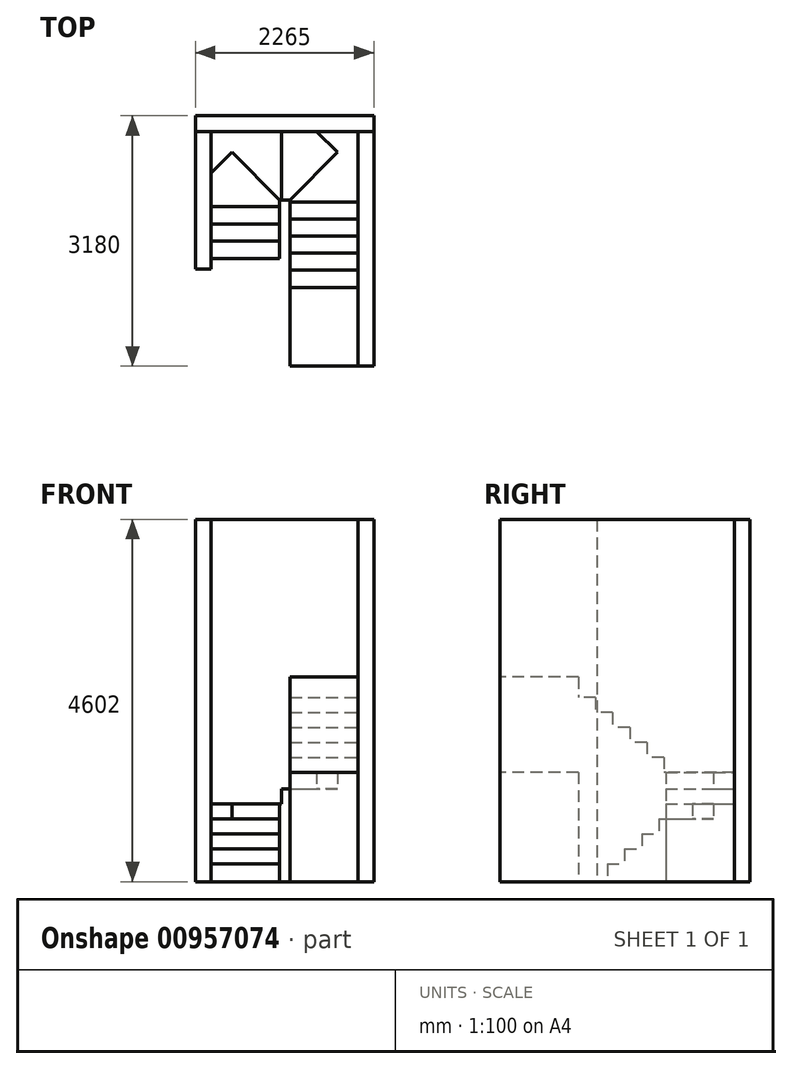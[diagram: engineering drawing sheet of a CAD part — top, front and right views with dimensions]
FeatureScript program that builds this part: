
annotation { "Feature Type Name" : "Feature", "Feature Type Description" : "" }
export const myFeature = defineFeature(function(context is Context, id is Id, definition is map)
    precondition{}
    {
        {
            var Q0;
            Q0=qCreatedBy(makeId("Top.planeOp"),FACE);
            var sketch = newSketch(context, id + "F0", { "sketchPlane" : qUnion([Q0])});
            skLineSegment(sketch, "E0", {"start": v(0, 0) * mm, "end": v(0, 1745) * mm});
            skLineSegment(sketch, "E1", {"start": v(0, 1745) * mm, "end": v(1865, 1745) * mm});
            skLineSegment(sketch, "E2", {"start": v(1865, 1745) * mm, "end": v(1865, -235) * mm});
            skLineSegment(sketch, "E3", {"start": v(870, 0) * mm, "end": v(870, 875) * mm});
            skLineSegment(sketch, "E4", {"start": v(870, 875) * mm, "end": v(1000, 875) * mm});
            skLineSegment(sketch, "E5", {"start": v(1000, 875) * mm, "end": v(1000, -235) * mm});
            skLineSegment(sketch, "E6", {"start": v(0, 130) * mm, "end": v(870, 130) * mm});
            skLineSegment(sketch, "E7", {"start": v(0, 350) * mm, "end": v(870, 350) * mm});
            skLineSegment(sketch, "E8", {"start": v(0, 570) * mm, "end": v(870, 570) * mm});
            skLineSegment(sketch, "E9", {"start": v(435, 130) * mm, "end": v(435, 350) * mm, "construction": true});
            skLineSegment(sketch, "E10", {"start": v(435, 350) * mm, "end": v(435, 570) * mm, "construction": true});
            skLineSegment(sketch, "E11", {"start": v(870, 790) * mm, "end": v(0, 790) * mm});
            skLineSegment(sketch, "E12", {"start": v(435, 570) * mm, "end": v(435, 790) * mm, "construction": true});
            skLineSegment(sketch, "E13", {"start": v(870, 875) * mm, "end": v(265, 1480) * mm});
            skLineSegment(sketch, "E14", {"start": v(265, 1480) * mm, "end": v(0, 1215) * mm});
            skLineSegment(sketch, "E15", {"start": v(895, 875) * mm, "end": v(895, 1745) * mm});
            skLineSegment(sketch, "E16", {"start": v(1000, 875) * mm, "end": v(1605, 1480) * mm});
            skLineSegment(sketch, "E17", {"start": v(1605, 1480) * mm, "end": v(1340, 1745) * mm});
            skLineSegment(sketch, "E18", {"start": v(1000, 850) * mm, "end": v(1865, 850) * mm});
            skLineSegment(sketch, "E19", {"start": v(1000, 633) * mm, "end": v(1865, 633) * mm});
            skLineSegment(sketch, "E20", {"start": v(1000, 416) * mm, "end": v(1865, 416) * mm});
            skLineSegment(sketch, "E21", {"start": v(1000, 199) * mm, "end": v(1865, 199) * mm});
            skLineSegment(sketch, "E22", {"start": v(1000, -18) * mm, "end": v(1865, -18) * mm});
            skLineSegment(sketch, "E23", {"start": v(1432.5, 850) * mm, "end": v(1432.5, 633) * mm, "construction": true});
            skLineSegment(sketch, "E24", {"start": v(1432.5, 633) * mm, "end": v(1432.5, 416) * mm, "construction": true});
            skLineSegment(sketch, "E25", {"start": v(1432.5, 416) * mm, "end": v(1432.5, 199) * mm, "construction": true});
            skLineSegment(sketch, "E26", {"start": v(1432.5, 199) * mm, "end": v(1432.5, -18) * mm, "construction": true});
            skLineSegment(sketch, "E27", {"start": v(1432.5, -18) * mm, "end": v(1432.5, -235) * mm, "construction": true});
            skLineSegment(sketch, "E28.trimOffspring", {"start": v(870, 0) * mm, "end": v(0, 0) * mm});
            skLineSegment(sketch, "E29", {"start": v(1000, -235) * mm, "end": v(1865, -235) * mm});
            skSolve(sketch);
        }
        {
            var Q0;
            {var subQ0=sQuery(id+"F0.wireOp",EDGE,"E13");Q0=makeQuery(id+"F0.imprint","IMPRINT",FACE,{"disambiguationData":[TD([[makeQuery(id+"F0.imprint","IMPRINT",EDGE,{"derivedFrom":subQ0}),-1.0]])]});}
            extrude(context, id + "F1", {"entities" : qUnion([Q0]), "depth" : 987 * mm, "offsetDistance" : 25 * mm});
        }
        {
            var Q0;
            {var subQ1=sQuery(id+"F0.wireOp",EDGE,"E11");Q0=makeQuery(id+"F0.imprint","IMPRINT",FACE,{"disambiguationData":[TD([[makeQuery(id+"F0.imprint","IMPRINT",EDGE,{"derivedFrom":subQ1}),-1.0]])]});}
            var Q1;
            Q1=makeQuery(id+"F1.opExtrude","CAP_FACE",FACE,{"disambiguationData":[OSD([sQuery(id+"F0.wireOp",EDGE,"E0"),sQuery(id+"F0.wireOp",EDGE,"E1"),sQuery(id+"F0.wireOp",EDGE,"E4"),sQuery(id+"F0.wireOp",EDGE,"E13"),sQuery(id+"F0.wireOp",EDGE,"E14"),sQuery(id+"F0.wireOp",EDGE,"E15")])],"isStart":false});
            extrude(context, id + "F2", {"entities" : qUnion([Q0]), "operationType" : NewBodyOperationType.ADD, "endBound" : BoundingType.UP_TO_SURFACE, "depth" : 25 * mm, "endBoundEntityFace" : qUnion([Q1]), "hasOffset" : true, "offsetDistance" : 190 * mm});
        }
        {
            var Q0;
            {var subQ0=sQuery(id+"F0.wireOp",EDGE,"E8");Q0=makeQuery(id+"F0.imprint","IMPRINT",FACE,{"disambiguationData":[TD([[makeQuery(id+"F0.imprint","IMPRINT",EDGE,{"derivedFrom":subQ0}),1.0]])]});}
            var Q1;
            Q1=makeQuery(id+"F2.opExtrude","CAP_FACE",FACE,{"disambiguationData":[OSD([sQuery(id+"F0.wireOp",EDGE,"E0"),sQuery(id+"F0.wireOp",EDGE,"E3"),sQuery(id+"F0.wireOp",EDGE,"E11"),sQuery(id+"F0.wireOp",EDGE,"E13"),sQuery(id+"F0.wireOp",EDGE,"E14")])],"isStart":false});
            extrude(context, id + "F3", {"entities" : qUnion([Q0]), "operationType" : NewBodyOperationType.ADD, "endBound" : BoundingType.UP_TO_SURFACE, "depth" : 25 * mm, "endBoundEntityFace" : qUnion([Q1]), "hasOffset" : true, "offsetDistance" : 190 * mm});
        }
        {
            var Q0;
            {var subQ0=sQuery(id+"F0.wireOp",EDGE,"E7");Q0=makeQuery(id+"F0.imprint","IMPRINT",FACE,{"disambiguationData":[TD([[makeQuery(id+"F0.imprint","IMPRINT",EDGE,{"derivedFrom":subQ0}),1.0]])]});}
            var Q1;
            Q1=makeQuery(id+"F3.opExtrude","CAP_FACE",FACE,{"disambiguationData":[OSD([sQuery(id+"F0.wireOp",EDGE,"E0"),sQuery(id+"F0.wireOp",EDGE,"E3"),sQuery(id+"F0.wireOp",EDGE,"E8"),sQuery(id+"F0.wireOp",EDGE,"E11")])],"isStart":false});
            extrude(context, id + "F4", {"entities" : qUnion([Q0]), "operationType" : NewBodyOperationType.ADD, "endBound" : BoundingType.UP_TO_SURFACE, "depth" : 25 * mm, "endBoundEntityFace" : qUnion([Q1]), "hasOffset" : true, "offsetDistance" : 190 * mm});
        }
        {
            var Q0;
            {var subQ0=sQuery(id+"F0.wireOp",EDGE,"E6");Q0=makeQuery(id+"F0.imprint","IMPRINT",FACE,{"disambiguationData":[TD([[makeQuery(id+"F0.imprint","IMPRINT",EDGE,{"derivedFrom":subQ0}),1.0]])]});}
            var Q1;
            Q1=makeQuery(id+"F4.opExtrude","CAP_FACE",FACE,{"disambiguationData":[OSD([sQuery(id+"F0.wireOp",EDGE,"E0"),sQuery(id+"F0.wireOp",EDGE,"E3"),sQuery(id+"F0.wireOp",EDGE,"E7"),sQuery(id+"F0.wireOp",EDGE,"E8")])],"isStart":false});
            extrude(context, id + "F5", {"entities" : qUnion([Q0]), "operationType" : NewBodyOperationType.ADD, "endBound" : BoundingType.UP_TO_SURFACE, "depth" : 25 * mm, "endBoundEntityFace" : qUnion([Q1]), "hasOffset" : true, "offsetDistance" : 190 * mm});
        }
        {
            var Q0;
            {var subQ1=sQuery(id+"F0.wireOp",EDGE,"E15");Q0=makeQuery(id+"F0.imprint","IMPRINT",FACE,{"disambiguationData":[TD([[makeQuery(id+"F0.imprint","IMPRINT",EDGE,{"derivedFrom":subQ1}),-1.0]])]});}
            var Q1;
            Q1=makeQuery(id+"F1.opExtrude","CAP_FACE",FACE,{"disambiguationData":[OSD([sQuery(id+"F0.wireOp",EDGE,"E0"),sQuery(id+"F0.wireOp",EDGE,"E1"),sQuery(id+"F0.wireOp",EDGE,"E4"),sQuery(id+"F0.wireOp",EDGE,"E13"),sQuery(id+"F0.wireOp",EDGE,"E14"),sQuery(id+"F0.wireOp",EDGE,"E15")])],"isStart":false});
            extrude(context, id + "F6", {"entities" : qUnion([Q0]), "operationType" : NewBodyOperationType.ADD, "endBound" : BoundingType.UP_TO_SURFACE, "depth" : 25 * mm, "endBoundEntityFace" : qUnion([Q1]), "hasOffset" : true, "offsetDistance" : 190 * mm, "offsetOppositeDirection" : true});
        }
        {
            var Q0;
            {var subQ0=sQuery(id+"F0.wireOp",EDGE,"E16");Q0=makeQuery(id+"F0.imprint","IMPRINT",FACE,{"disambiguationData":[TD([[makeQuery(id+"F0.imprint","IMPRINT",EDGE,{"derivedFrom":subQ0}),-1.0]])]});}
            var Q1;
            Q1=makeQuery(id+"F1.opExtrude","CAP_FACE",FACE,{"disambiguationData":[OSD([sQuery(id+"F0.wireOp",EDGE,"E0"),sQuery(id+"F0.wireOp",EDGE,"E1"),sQuery(id+"F0.wireOp",EDGE,"E4"),sQuery(id+"F0.wireOp",EDGE,"E13"),sQuery(id+"F0.wireOp",EDGE,"E14"),sQuery(id+"F0.wireOp",EDGE,"E15")])],"isStart":false});
            extrude(context, id + "F7", {"entities" : qUnion([Q0]), "operationType" : NewBodyOperationType.ADD, "endBound" : BoundingType.UP_TO_SURFACE, "depth" : 25 * mm, "endBoundEntityFace" : qUnion([Q1]), "hasOffset" : true, "offsetDistance" : 405 * mm, "offsetOppositeDirection" : true});
        }
        {
            var Q0;
            {var subQ0=sQuery(id+"F0.wireOp",EDGE,"E18");Q0=makeQuery(id+"F0.imprint","IMPRINT",FACE,{"disambiguationData":[TD([[makeQuery(id+"F0.imprint","IMPRINT",EDGE,{"derivedFrom":subQ0}),-1.0]])]});}
            var Q1;
            Q1=makeQuery(id+"F7.opExtrude","CAP_FACE",FACE,{"disambiguationData":[OSD([sQuery(id+"F0.wireOp",EDGE,"E1"),sQuery(id+"F0.wireOp",EDGE,"E2"),sQuery(id+"F0.wireOp",EDGE,"E5"),sQuery(id+"F0.wireOp",EDGE,"E16"),sQuery(id+"F0.wireOp",EDGE,"E17"),sQuery(id+"F0.wireOp",EDGE,"E18")])],"isStart":false});
            extrude(context, id + "F8", {"entities" : qUnion([Q0]), "operationType" : NewBodyOperationType.ADD, "endBound" : BoundingType.UP_TO_SURFACE, "depth" : 25 * mm, "endBoundEntityFace" : qUnion([Q1]), "hasOffset" : true, "offsetDistance" : 190 * mm, "offsetOppositeDirection" : true});
        }
        {
            var Q0;
            {var subQ0=sQuery(id+"F0.wireOp",EDGE,"E19");Q0=makeQuery(id+"F0.imprint","IMPRINT",FACE,{"disambiguationData":[TD([[makeQuery(id+"F0.imprint","IMPRINT",EDGE,{"derivedFrom":subQ0}),-1.0]])]});}
            var Q1;
            Q1=makeQuery(id+"F8.opExtrude","CAP_FACE",FACE,{"disambiguationData":[OSD([sQuery(id+"F0.wireOp",EDGE,"E2"),sQuery(id+"F0.wireOp",EDGE,"E5"),sQuery(id+"F0.wireOp",EDGE,"E18"),sQuery(id+"F0.wireOp",EDGE,"E19")])],"isStart":false});
            extrude(context, id + "F9", {"entities" : qUnion([Q0]), "operationType" : NewBodyOperationType.ADD, "endBound" : BoundingType.UP_TO_SURFACE, "depth" : 25 * mm, "endBoundEntityFace" : qUnion([Q1]), "hasOffset" : true, "offsetDistance" : 190 * mm, "offsetOppositeDirection" : true});
        }
        {
            var Q0;
            {var subQ0=sQuery(id+"F0.wireOp",EDGE,"E20");Q0=makeQuery(id+"F0.imprint","IMPRINT",FACE,{"disambiguationData":[TD([[makeQuery(id+"F0.imprint","IMPRINT",EDGE,{"derivedFrom":subQ0}),-1.0]])]});}
            var Q1;
            Q1=makeQuery(id+"F9.opExtrude","CAP_FACE",FACE,{"disambiguationData":[OSD([sQuery(id+"F0.wireOp",EDGE,"E2"),sQuery(id+"F0.wireOp",EDGE,"E5"),sQuery(id+"F0.wireOp",EDGE,"E19"),sQuery(id+"F0.wireOp",EDGE,"E20")])],"isStart":false});
            extrude(context, id + "F10", {"entities" : qUnion([Q0]), "operationType" : NewBodyOperationType.ADD, "endBound" : BoundingType.UP_TO_SURFACE, "depth" : 25 * mm, "endBoundEntityFace" : qUnion([Q1]), "hasOffset" : true, "offsetDistance" : 190 * mm, "offsetOppositeDirection" : true});
        }
        {
            var Q0;
            {var subQ0=sQuery(id+"F0.wireOp",EDGE,"E21");Q0=makeQuery(id+"F0.imprint","IMPRINT",FACE,{"disambiguationData":[TD([[makeQuery(id+"F0.imprint","IMPRINT",EDGE,{"derivedFrom":subQ0}),-1.0]])]});}
            var Q1;
            Q1=makeQuery(id+"F10.opExtrude","CAP_FACE",FACE,{"disambiguationData":[OSD([sQuery(id+"F0.wireOp",EDGE,"E2"),sQuery(id+"F0.wireOp",EDGE,"E5"),sQuery(id+"F0.wireOp",EDGE,"E20"),sQuery(id+"F0.wireOp",EDGE,"E21")])],"isStart":false});
            extrude(context, id + "F11", {"entities" : qUnion([Q0]), "operationType" : NewBodyOperationType.ADD, "endBound" : BoundingType.UP_TO_SURFACE, "depth" : 25 * mm, "endBoundEntityFace" : qUnion([Q1]), "hasOffset" : true, "offsetDistance" : 190 * mm, "offsetOppositeDirection" : true});
        }
        {
            var Q0;
            {var subQ2=sQuery(id+"F0.wireOp",EDGE,"E22");Q0=makeQuery(id+"F0.imprint","IMPRINT",FACE,{"disambiguationData":[TD([[makeQuery(id+"F0.imprint","IMPRINT",EDGE,{"derivedFrom":subQ2}),-1.0]])]});}
            var Q1;
            Q1=makeQuery(id+"F11.opExtrude","CAP_FACE",FACE,{"disambiguationData":[OSD([sQuery(id+"F0.wireOp",EDGE,"E2"),sQuery(id+"F0.wireOp",EDGE,"E5"),sQuery(id+"F0.wireOp",EDGE,"E21"),sQuery(id+"F0.wireOp",EDGE,"E22")])],"isStart":false});
            extrude(context, id + "F12", {"entities" : qUnion([Q0]), "operationType" : NewBodyOperationType.ADD, "endBound" : BoundingType.UP_TO_SURFACE, "depth" : 25 * mm, "endBoundEntityFace" : qUnion([Q1]), "hasOffset" : true, "offsetDistance" : 190 * mm, "offsetOppositeDirection" : true});
        }
        {
            var Q0;
            Q0=makeQuery(id+"F7.opExtrude","CAP_FACE",FACE,{"disambiguationData":[OSD([sQuery(id+"F0.wireOp",EDGE,"E1"),sQuery(id+"F0.wireOp",EDGE,"E2"),sQuery(id+"F0.wireOp",EDGE,"E5"),sQuery(id+"F0.wireOp",EDGE,"E16"),sQuery(id+"F0.wireOp",EDGE,"E17"),sQuery(id+"F0.wireOp",EDGE,"E18")])],"isStart":false});
            var sketch = newSketch(context, id + "F13", { "sketchPlane" : qUnion([Q0])});
            skLineSegment(sketch, "E30.bottom", {"start": v(1865, -235) * mm, "end": v(1000, -235) * mm});
            skLineSegment(sketch, "E30.top", {"start": v(1865, -1235) * mm, "end": v(1000, -1235) * mm});
            skLineSegment(sketch, "E30.left", {"start": v(1865, -235) * mm, "end": v(1865, -1235) * mm});
            skLineSegment(sketch, "E30.right", {"start": v(1000, -235) * mm, "end": v(1000, -1235) * mm});
            skSolve(sketch);
        }
        {
            var Q0;
            Q0 = qSketchRegion(id + "F13", true);
            extrude(context, id + "F14", {"entities" : qUnion([Q0]), "operationType" : NewBodyOperationType.ADD, "depth" : 1210 * mm, "offsetDistance" : 25 * mm});
        }
        {
            var Q0;
            Q0=qCreatedBy(makeId("Top.planeOp"),FACE);
            var sketch = newSketch(context, id + "F15", { "sketchPlane" : qUnion([Q0])});
            skLineSegment(sketch, "E31.bottom", {"start": v(0, 1745) * mm, "end": v(-200, 1745) * mm});
            skLineSegment(sketch, "E31.top", {"start": v(0, 0) * mm, "end": v(-200, 0) * mm});
            skLineSegment(sketch, "E31.left", {"start": v(0, 1745) * mm, "end": v(0, 0) * mm});
            skLineSegment(sketch, "E31.right", {"start": v(-200, 1745) * mm, "end": v(-200, 0) * mm});
            skSolve(sketch);
        }
        {
            var Q0;
            Q0 = qSketchRegion(id + "F15", true);
            var Q1;
            Q1=makeQuery(id+"F14.opExtrude","CAP_FACE",FACE,{"disambiguationData":[OSD([sQuery(id+"F13.wireOp",EDGE,"E30.bottom"),sQuery(id+"F13.wireOp",EDGE,"E30.top"),sQuery(id+"F13.wireOp",EDGE,"E30.left"),sQuery(id+"F13.wireOp",EDGE,"E30.right")])],"isStart":false});
            extrude(context, id + "F16", {"entities" : qUnion([Q0]), "endBound" : BoundingType.UP_TO_SURFACE, "depth" : 25 * mm, "endBoundEntityFace" : qUnion([Q1]), "hasOffset" : true, "offsetDistance" : 2000 * mm, "offsetOppositeDirection" : true});
        }
        {
            var Q0;
            Q0=qCreatedBy(makeId("Top.planeOp"),FACE);
            var sketch = newSketch(context, id + "F17", { "sketchPlane" : qUnion([Q0])});
            skLineSegment(sketch, "E32.bottom", {"start": v(1865, -1235) * mm, "end": v(2065, -1235) * mm});
            skLineSegment(sketch, "E32.top", {"start": v(1865, 1745) * mm, "end": v(2065, 1745) * mm});
            skLineSegment(sketch, "E32.left", {"start": v(1865, -1235) * mm, "end": v(1865, 1745) * mm});
            skLineSegment(sketch, "E32.right", {"start": v(2065, -1235) * mm, "end": v(2065, 1745) * mm});
            skSolve(sketch);
        }
        {
            var Q0;
            Q0 = qSketchRegion(id + "F17", true);
            var Q1;
            Q1=makeQuery(id+"F16.opExtrude","CAP_FACE",FACE,{"disambiguationData":[OSD([sQuery(id+"F15.wireOp",EDGE,"E31.bottom"),sQuery(id+"F15.wireOp",EDGE,"E31.top"),sQuery(id+"F15.wireOp",EDGE,"E31.left"),sQuery(id+"F15.wireOp",EDGE,"E31.right")])],"isStart":false});
            extrude(context, id + "F18", {"entities" : qUnion([Q0]), "endBound" : BoundingType.UP_TO_SURFACE, "depth" : 25 * mm, "endBoundEntityFace" : qUnion([Q1]), "offsetDistance" : 25 * mm});
        }
        {
            var Q0;
            Q0=qCreatedBy(makeId("Top.planeOp"),FACE);
            var sketch = newSketch(context, id + "F19", { "sketchPlane" : qUnion([Q0])});
            skLineSegment(sketch, "E33.bottom", {"start": v(-200, 1745) * mm, "end": v(2065, 1745) * mm});
            skLineSegment(sketch, "E33.top", {"start": v(-200, 1945) * mm, "end": v(2065, 1945) * mm});
            skLineSegment(sketch, "E33.left", {"start": v(-200, 1745) * mm, "end": v(-200, 1945) * mm});
            skLineSegment(sketch, "E33.right", {"start": v(2065, 1745) * mm, "end": v(2065, 1945) * mm});
            skSolve(sketch);
        }
        {
            var Q0;
            Q0 = qSketchRegion(id + "F19", true);
            var Q1;
            Q1=makeQuery(id+"F18.opExtrude","CAP_FACE",FACE,{"disambiguationData":[OSD([sQuery(id+"F17.wireOp",EDGE,"E32.bottom"),sQuery(id+"F17.wireOp",EDGE,"E32.top"),sQuery(id+"F17.wireOp",EDGE,"E32.left"),sQuery(id+"F17.wireOp",EDGE,"E32.right")])],"isStart":false});
            extrude(context, id + "F20", {"entities" : qUnion([Q0]), "endBound" : BoundingType.UP_TO_SURFACE, "depth" : 25 * mm, "endBoundEntityFace" : qUnion([Q1]), "offsetDistance" : 25 * mm});
        }
        {
            var Q0;
            Q0=makeQuery(id+"F20.opExtrude","SWEPT_FACE",FACE,{"disambiguationData":[OSD([sQuery(id+"F19.wireOp",EDGE,"E33.bottom")])]});
            var sketch = newSketch(context, id + "F21", { "sketchPlane" : qUnion([Q0])});
            skSolve(sketch);
        }
        {
            var Q0;
            {var subQ0=sQuery(id+"F19.wireOp",EDGE,"E33.bottom");Q0=makeQuery(id+"F21.imprint","IMPRINT",FACE,{"disambiguationData":[TD([[makeQuery(id+"F21.imprint","IMPRINT",EDGE,{"derivedFrom":makeQuery(id+"F20.opExtrude","CAP_EDGE",EDGE,{"disambiguationData":[OSD([subQ0])],"isStart":true})}),1.0]])]});}
            cPlane(context, id + "F22", {"entities" : qUnion([Q0]), "cplaneType" : CPlaneType.OFFSET, "offset" : 65 * mm, "width" : 150 * mm, "height" : 150 * mm});
        }
        {
            var Q0;
            Q0=makeQuery(id+"F16.opExtrude","SWEPT_FACE",FACE,{"disambiguationData":[OSD([sQuery(id+"F15.wireOp",EDGE,"E31.left")])]});
            cPlane(context, id + "F23", {"entities" : qUnion([Q0]), "cplaneType" : CPlaneType.OFFSET, "offset" : 65 * mm, "width" : 150 * mm, "height" : 150 * mm});
        }
        {
            var Q0;
            Q0=makeQuery(id+"F18.opExtrude","SWEPT_FACE",FACE,{"disambiguationData":[OSD([sQuery(id+"F17.wireOp",EDGE,"E32.left")])]});
            cPlane(context, id + "F24", {"entities" : qUnion([Q0]), "cplaneType" : CPlaneType.OFFSET, "offset" : 65 * mm, "width" : 150 * mm, "height" : 150 * mm});
        }
    });
